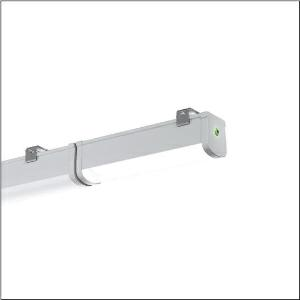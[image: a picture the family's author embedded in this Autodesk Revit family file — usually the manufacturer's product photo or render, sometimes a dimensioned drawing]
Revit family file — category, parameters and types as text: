
# Revit family: monsun_r__31_58fa207a403b3g_c1e4
name_source: partatom
category: Lighting Fixtures
units: mm (PartAtom-declared; Revit-internal decimal feet)

## family parameters
Cut with Voids When Loaded = No
Host = Face
Light Source = No
Part Type = Normal
Room Calculation Point = No
Round Connector Dimension = Use Diameter
Shared = No

## types (1)
- --- (1 x LED, 450 lm, 5 W, 4000K)
    Apparent Load = 5 VA
    CIE Flux Codes = 42 72 91 92 100
    Color Rendering = 80
    Color Temperature = 4000K
    Default Elevation = 1800 mm
    Description = Monsun® 31, emergency light element, primary optical cover: diffuser, of PC, frosted, light emission: direct distribution, primary light characteristic: symmetric, installation type: surface-mounted, EM-KIT 3h,LED, rated luminous flux: 450lm, luminous efficacy: 100lm/W, light colour: 840, colour temperature: 4000K, control gear: without control gear, emergency light function, with socket/plug, mains connection: 220..240V, AC, 50..60Hz, rated input power: 5W, housing, luminaire housing, of PC, light grey (RAL 7035), length: 297mm, width: 68mm, height: 76mm, protection rating (complete): IP65, insulation class (complete): insulation class II (safety insulation), certification: CE, protection symbol: D, impact resistance: IK08, permissible operating ambient temperature: 0..+40°C, standard: EN 60598-2-22, corresponds to IFS (International Featured Standards) requirements for safety and quality in the food industry, packaging unit: 1 piece
    Height = 77 mm
    Lamp = 1 x LED
    Lamp Light Flux = 450 lm
    Lamp Power = 5 W
    Lamp count = 1
    Length = 294 mm
    Luminous efficacy = 90 lm/W
    Manufacturer = Siteco
    ModVariant = No
    Model = 58FA207A403B3G
    Mounting Place = Ceiling
    Mounting Type = Surface mounted
    Number of Poles = 1
    OnlyDefault = Yes
    Power Factor = 1
    Product Name = Monsun® 31
    Product group = emergency light element
    ProductGroupID = 306
    Protection Class = Protection class II
    Protection Degree = IP 65
    RLX_Detail_Level = 1
    RLX_Emergency_Light_Flux = 0 lm
    RLX_Emergency_Type = 0
    RLX_Emergency_Type_DB = No
    RlxData = <blob elided: 31121 chars, md5=f6738ea3>
    Socket = socket
    Standby Power = 0 W
    System Light Flux = 450 lm
    System Power = 5 W
    Type Comments = : 3 h
    Type Image = l_1006658.jpg
    URL = http://relux.com
    VarID = @adj_136695
    Voltage = 0 V
    Weight = 0.00 kg
    Width = 69 mm

## geometry (parser evidence)
native form markers: Blend x4, Sweep x11
no freeform markers — native parametric forms only
